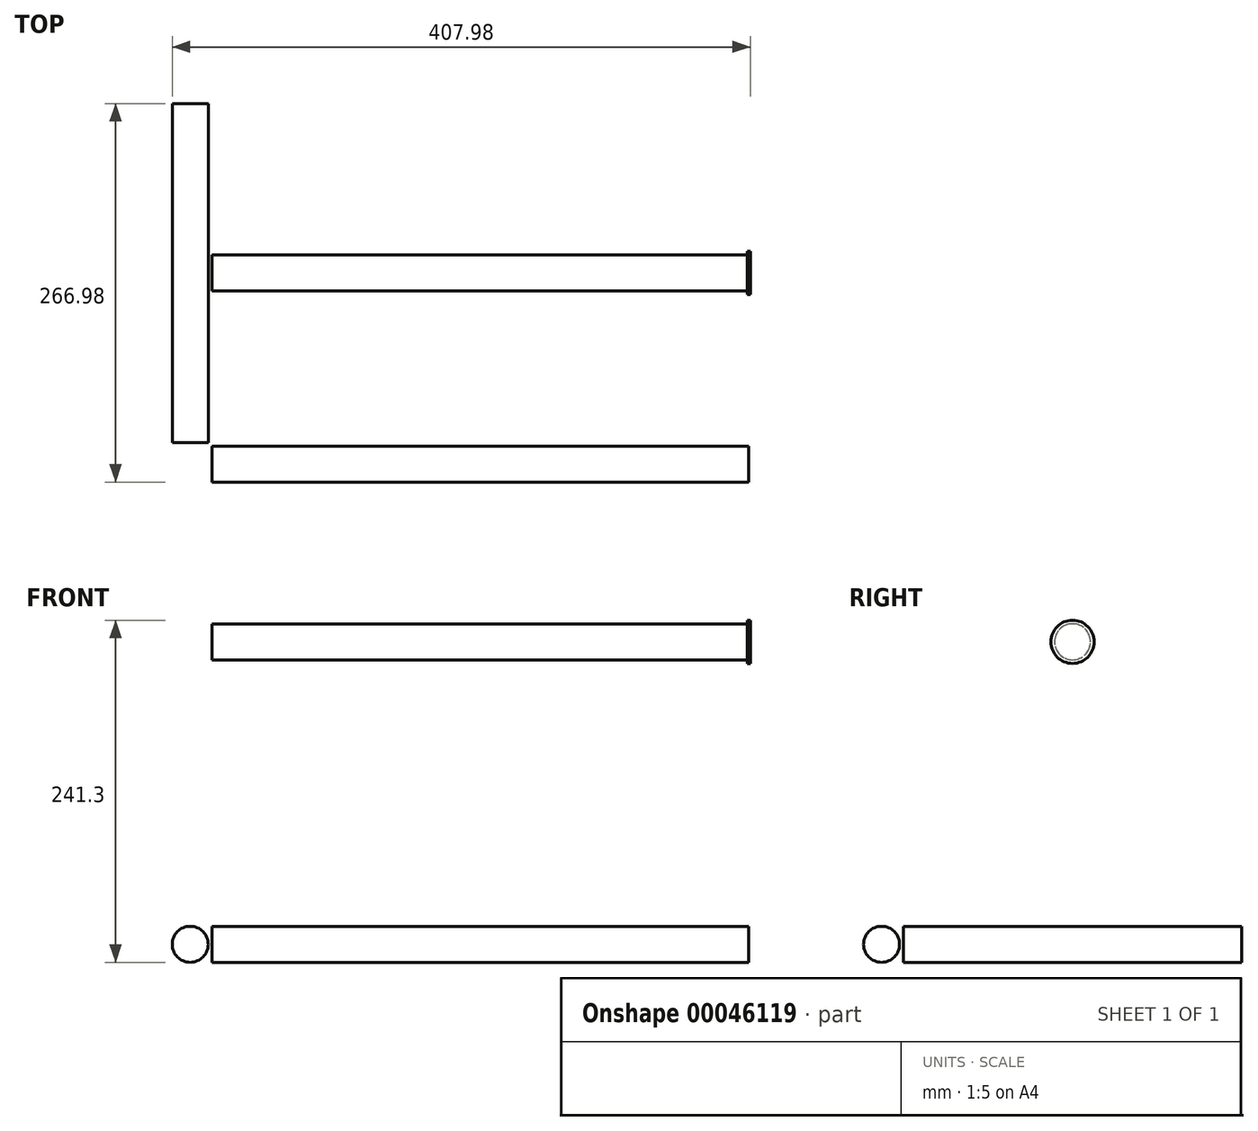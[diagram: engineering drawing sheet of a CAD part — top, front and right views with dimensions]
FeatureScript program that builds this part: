
annotation { "Feature Type Name" : "Feature", "Feature Type Description" : "" }
export const myFeature = defineFeature(function(context is Context, id is Id, definition is map)
    precondition{}
    {
        {
            assignVariable(context, id + "F0", {"name" : "pipe", "anyValue" : 1});
        }
        {
            var Q0;
            Q0=qCreatedBy(makeId("Top.planeOp"),FACE);
            var sketch = newSketch(context, id + "F1", { "sketchPlane" : qUnion([Q0])});
            skLineSegment(sketch, "E0.rect.bottom", {"start": v(220, -150) * mm, "end": v(-220, -150) * mm, "construction": true});
            skLineSegment(sketch, "E0.rect.top", {"start": v(220, 150) * mm, "end": v(-220, 150) * mm, "construction": true});
            skLineSegment(sketch, "E0.rect.left", {"start": v(220, -150) * mm, "end": v(220, 150) * mm, "construction": true});
            skLineSegment(sketch, "E0.rect.right", {"start": v(-220, -150) * mm, "end": v(-220, 150) * mm, "construction": true});
            skPoint(sketch, "E0.rect.middle", {"position": v(0, 0) * mm});
            skLineSegment(sketch, "E1.bottom", {"start": v(-220, -150) * mm, "end": v(-189.52, -150) * mm});
            skLineSegment(sketch, "E1.top", {"start": v(-220, -119.52) * mm, "end": v(-189.52, -119.52) * mm});
            skLineSegment(sketch, "E1.left", {"start": v(-220, -150) * mm, "end": v(-220, -119.52) * mm});
            skLineSegment(sketch, "E1.right", {"start": v(-189.52, -150) * mm, "end": v(-189.52, -119.52) * mm});
            skLineSegment(sketch, "E2.bottom", {"start": v(-220, 150) * mm, "end": v(-189.52, 150) * mm});
            skLineSegment(sketch, "E2.top", {"start": v(-220, 119.52) * mm, "end": v(-189.52, 119.52) * mm});
            skLineSegment(sketch, "E2.left", {"start": v(-220, 150) * mm, "end": v(-220, 119.52) * mm});
            skLineSegment(sketch, "E2.right", {"start": v(-189.52, 150) * mm, "end": v(-189.52, 119.52) * mm});
            skLineSegment(sketch, "E3.bottom", {"start": v(220, 150) * mm, "end": v(189.52, 150) * mm});
            skLineSegment(sketch, "E3.top", {"start": v(220, 119.52) * mm, "end": v(189.52, 119.52) * mm});
            skLineSegment(sketch, "E3.left", {"start": v(220, 150) * mm, "end": v(220, 119.52) * mm});
            skLineSegment(sketch, "E3.right", {"start": v(189.52, 150) * mm, "end": v(189.52, 119.52) * mm});
            skLineSegment(sketch, "E4.bottom", {"start": v(220, -150) * mm, "end": v(189.52, -150) * mm});
            skLineSegment(sketch, "E4.top", {"start": v(220, -119.52) * mm, "end": v(189.52, -119.52) * mm});
            skLineSegment(sketch, "E4.left", {"start": v(220, -150) * mm, "end": v(220, -119.52) * mm});
            skLineSegment(sketch, "E4.right", {"start": v(189.52, -150) * mm, "end": v(189.52, -119.52) * mm});
            skSolve(sketch);
        }
        {
            var Q0;
            Q0=qCreatedBy(makeId("Right.planeOp"),FACE);
            var Q1;
            Q1=sQuery(id+"F1.wireOp",EDGE,"E1.right");
            cPlane(context, id + "F2", {"entities" : qUnion([Q0, Q1]), "cplaneType" : CPlaneType.LINE_ANGLE, "offset" : 152.4 * mm, "angle" : 0 * degree, "width" : 152.4 * mm, "height" : 152.4 * mm});
        }
        {
            var Q0;
            Q0=sQuery(id+"F1.wireOp",EDGE,"E1.top");
            var Q1;
            Q1=qCreatedBy(makeId("Front.planeOp"),FACE);
            cPlane(context, id + "F3", {"entities" : qUnion([Q0, Q1]), "cplaneType" : CPlaneType.LINE_ANGLE, "offset" : 152.4 * mm, "angle" : 0 * degree, "width" : 152.4 * mm, "height" : 152.4 * mm});
        }
        {
            var Q0;
            Q0=sQuery(id+"F1.wireOp",EDGE,"E3.right");
            var Q1;
            Q1=qCreatedBy(makeId("Right.planeOp"),FACE);
            cPlane(context, id + "F4", {"entities" : qUnion([Q0, Q1]), "cplaneType" : CPlaneType.LINE_ANGLE, "offset" : 152.4 * mm, "angle" : 0 * degree, "width" : 152.4 * mm, "height" : 152.4 * mm});
        }
        {
            var Q0;
            Q0=sQuery(id+"F1.wireOp",EDGE,"E3.top");
            var Q1;
            Q1=qCreatedBy(makeId("Front.planeOp"),FACE);
            cPlane(context, id + "F5", {"entities" : qUnion([Q0, Q1]), "cplaneType" : CPlaneType.LINE_ANGLE, "offset" : 152.4 * mm, "angle" : 0 * degree, "width" : 152.4 * mm, "height" : 152.4 * mm});
        }
        {
            var Q0;
            Q0=qCreatedBy(makeId("Right.planeOp"),FACE);
            var sketch = newSketch(context, id + "F6", { "sketchPlane" : qUnion([Q0])});
            skCircle(sketch, "E5", {"center": v(-134.76, 15.24) * mm, "radius": 12.7 * mm});
            skLineSegment(sketch, "E6", {"start": v(-134.76, 15.24) * mm, "end": v(-134.76, 0) * mm, "construction": true});
            skLineSegment(sketch, "E7.0", {"start": v(-150, 0) * mm, "end": v(-119.52, 0) * mm});
            skSolve(sketch);
        }
        {
            var Q0;
            Q0=makeQuery(id+"F6.imprint","IMPRINT",FACE,{"disambiguationData":[TD([[makeQuery(id+"F6.imprint","IMPRINT",EDGE,{"derivedFrom":sQuery(id+"F6.wireOp",EDGE,"E5")}),1.0]])]});
            var Q1;
            Q1=qCreatedBy(id+"F4.planeOp",FACE);
            var Q2;
            Q2=qCreatedBy(id+"F2.planeOp",FACE);
            extrude(context, id + "F7", {"entities" : qUnion([Q0]), "endBound" : BoundingType.UP_TO_SURFACE, "endBoundEntityFace" : qUnion([Q1]), "depth" : 25.4 * mm, "hasSecondDirection" : true, "secondDirectionBound" : SecondDirectionBoundingType.UP_TO_SURFACE, "secondDirectionOppositeDirection" : true, "secondDirectionBoundEntityFace" : qUnion([Q2]), "secondDirectionDepth" : 25.4 * mm});
        }
        {
            var Q0;
            Q0=qCreatedBy(makeId("Front.planeOp"),FACE);
            var sketch = newSketch(context, id + "F8", { "sketchPlane" : qUnion([Q0])});
            skCircle(sketch, "E8", {"center": v(-204.76, 15.24) * mm, "radius": 12.7 * mm});
            skLineSegment(sketch, "E9", {"start": v(0, 0) * mm, "end": v(0, 35.46) * mm, "construction": true});
            skCircle(sketch, "E10.MirrorC", {"center": v(204.76, 15.24) * mm, "radius": 12.7 * mm});
            skSolve(sketch);
        }
        {
            var Q0;
            Q0=makeQuery(id+"F8.imprint","IMPRINT",FACE,{"disambiguationData":[TD([[makeQuery(id+"F8.imprint","IMPRINT",EDGE,{"derivedFrom":sQuery(id+"F8.wireOp",EDGE,"E10.MirrorC")}),-1.0]])]});
            var Q1;
            Q1=makeQuery(id+"F8.imprint","IMPRINT",FACE,{"disambiguationData":[TD([[makeQuery(id+"F8.imprint","IMPRINT",EDGE,{"derivedFrom":sQuery(id+"F8.wireOp",EDGE,"E8")}),1.0]])]});
            var Q2;
            Q2=qCreatedBy(id+"F3.planeOp",FACE);
            var Q3;
            Q3=qCreatedBy(id+"F5.planeOp",FACE);
            extrude(context, id + "F9", {"entities" : qUnion([Q0, Q1]), "endBound" : BoundingType.UP_TO_SURFACE, "endBoundEntityFace" : qUnion([Q2]), "depth" : 25.4 * mm, "hasSecondDirection" : true, "secondDirectionBound" : SecondDirectionBoundingType.UP_TO_SURFACE, "secondDirectionOppositeDirection" : true, "secondDirectionBoundEntityFace" : qUnion([Q3]), "secondDirectionDepth" : 25.4 * mm});
        }
        {
            var Q0;
            Q0=qCreatedBy(makeId("Right.planeOp"),FACE);
            var sketch = newSketch(context, id + "F10", { "sketchPlane" : qUnion([Q0])});
            skLineSegment(sketch, "E11", {"start": v(-150, 127) * mm, "end": v(150, 127) * mm, "construction": true});
            skLineSegment(sketch, "E12", {"start": v(0, 0) * mm, "end": v(0, 312.98) * mm, "construction": true});
            skCircle(sketch, "E13", {"center": v(0, 222.25) * mm, "radius": 95.25 * mm});
            skCircle(sketch, "E14", {"center": v(0, 222.25) * mm, "radius": 19.05 * mm});
            skCircle(sketch, "E15", {"center": v(0, 228.6) * mm, "radius": 12.7 * mm});
            skLineSegment(sketch, "E16", {"start": v(-43.67, 241.3) * mm, "end": v(37.44, 241.3) * mm, "construction": true});
            skSolve(sketch);
        }
        {
            var Q0;
            Q0=makeQuery(id+"F10.imprint","IMPRINT",FACE,{"disambiguationData":[TD([[makeQuery(id+"F10.imprint","IMPRINT",EDGE,{"derivedFrom":sQuery(id+"F10.wireOp",EDGE,"E15")}),1.0]])]});
            var Q1;
            Q1=qCreatedBy(id+"F4.planeOp",FACE);
            var Q2;
            Q2=qCreatedBy(id+"F2.planeOp",FACE);
            extrude(context, id + "F11", {"entities" : qUnion([Q0]), "endBound" : BoundingType.UP_TO_SURFACE, "endBoundEntityFace" : qUnion([Q1]), "depth" : 25.4 * mm, "hasSecondDirection" : true, "secondDirectionBound" : SecondDirectionBoundingType.UP_TO_SURFACE, "secondDirectionOppositeDirection" : true, "secondDirectionBoundEntityFace" : qUnion([Q2]), "secondDirectionDepth" : 25.4 * mm});
        }
        {
            var Q0;
            Q0=makeQuery(id+"F11.opExtrude","CAP_FACE",FACE,{"disambiguationData":[OSD([sQuery(id+"F10.wireOp",EDGE,"E15")])],"isStart":false});
            var sketch = newSketch(context, id + "F12", { "sketchPlane" : qUnion([Q0])});
            skCircle(sketch, "E17.0.0", {"center": v(0, 228.6) * mm, "radius": 12.7 * mm});
            skCircle(sketch, "E18", {"center": v(0, 228.6) * mm, "radius": 15.24 * mm});
            skSolve(sketch);
        }
        {
            var Q0;
            Q0=makeQuery(id+"F12.imprint","IMPRINT",FACE,{"disambiguationData":[TD([[makeQuery(id+"F12.imprint","IMPRINT",EDGE,{"derivedFrom":sQuery(id+"F12.wireOp",EDGE,"E17.0.0")}),1.0]])]});
            extrude(context, id + "F13", {"entities" : qUnion([Q0]), "oppositeDirection" : true, "depth" : (getVariable(context, 'pipe')) * mm});
        }
        {
            var Q0;
            Q0=makeQuery(id+"F12.imprint","IMPRINT",FACE,{"disambiguationData":[TD([[makeQuery(id+"F12.imprint","IMPRINT",EDGE,{"derivedFrom":sQuery(id+"F12.wireOp",EDGE,"E17.0.0")}),-1.0]])]});
            var Q1;
            Q1=makeQuery(id+"F12.imprint","IMPRINT",FACE,{"disambiguationData":[TD([[makeQuery(id+"F12.imprint","IMPRINT",EDGE,{"derivedFrom":sQuery(id+"F12.wireOp",EDGE,"E17.0.0")}),1.0]])]});
            extrude(context, id + "F14", {"entities" : qUnion([Q0, Q1]), "operationType" : NewBodyOperationType.ADD, "depth" : (getVariable(context, 'pipe')) * mm});
        }
        {
            var Q0;
            Q0=qCreatedBy(makeId("Top.planeOp"),FACE);
            var sketch = newSketch(context, id + "F15", { "sketchPlane" : qUnion([Q0])});
            skLineSegment(sketch, "E19.0", {"start": v(189.52, 15.24) * mm, "end": v(189.52, -15.24) * mm});
            skLineSegment(sketch, "E20.0", {"start": v(214.92, 15.24) * mm, "end": v(214.92, -15.24) * mm});
            skLineSegment(sketch, "E21", {"start": v(189.52, 15.24) * mm, "end": v(214.92, 15.24) * mm});
            skLineSegment(sketch, "E22", {"start": v(214.92, -15.24) * mm, "end": v(189.52, -15.24) * mm});
            skCircle(sketch, "E23", {"center": v(202.22, 0) * mm, "radius": 6.35 * mm});
            skPoint(sketch, "E24", {"position": v(202.22, 15.24) * mm});
            skCircle(sketch, "E25", {"center": v(202.22, 0) * mm, "radius": 15.24 * mm});
            skSolve(sketch);
        }
        {
            var Q0;
            Q0=makeQuery(id+"F15.imprint","IMPRINT",FACE,{"disambiguationData":[TD([[makeQuery(id+"F15.imprint","IMPRINT",EDGE,{"derivedFrom":sQuery(id+"F15.wireOp",EDGE,"E23")}),1.0]])]});
            var Q1;
            {var subQ0=sQuery(id+"F15.wireOp",EDGE,"E21");var subQ1=sQuery(id+"F15.wireOp",EDGE,"E20.0");var subQ2=makeQuery(id+"F15.imprint","INTERSECT",VERTEX,{"derivedFrom":[subQ1,subQ0]});Q1=makeQuery(id+"F15.imprint","IMPRINT",FACE,{"disambiguationData":[TD([[makeQuery(id+"F15.imprint","IMPRINT",EDGE,{"disambiguationData":[TD([[subQ2,-1.0]])],"derivedFrom":subQ1}),-1.0]])]});}
            var Q2;
            {var subQ0=sQuery(id+"F15.wireOp",EDGE,"E22");var subQ1=sQuery(id+"F15.wireOp",EDGE,"E20.0");var subQ2=makeQuery(id+"F15.imprint","INTERSECT",VERTEX,{"derivedFrom":[subQ1,subQ0]});Q2=makeQuery(id+"F15.imprint","IMPRINT",FACE,{"disambiguationData":[TD([[makeQuery(id+"F15.imprint","IMPRINT",EDGE,{"disambiguationData":[TD([[subQ2,1.0]])],"derivedFrom":subQ1}),-1.0]])]});}
            extrude(context, id + "F16", {"entities" : qUnion([Q0, Q1, Q2]), "operationType" : NewBodyOperationType.REMOVE, "endBound" : BoundingType.THROUGH_ALL, "depth" : 221.05 * mm});
        }
    });
